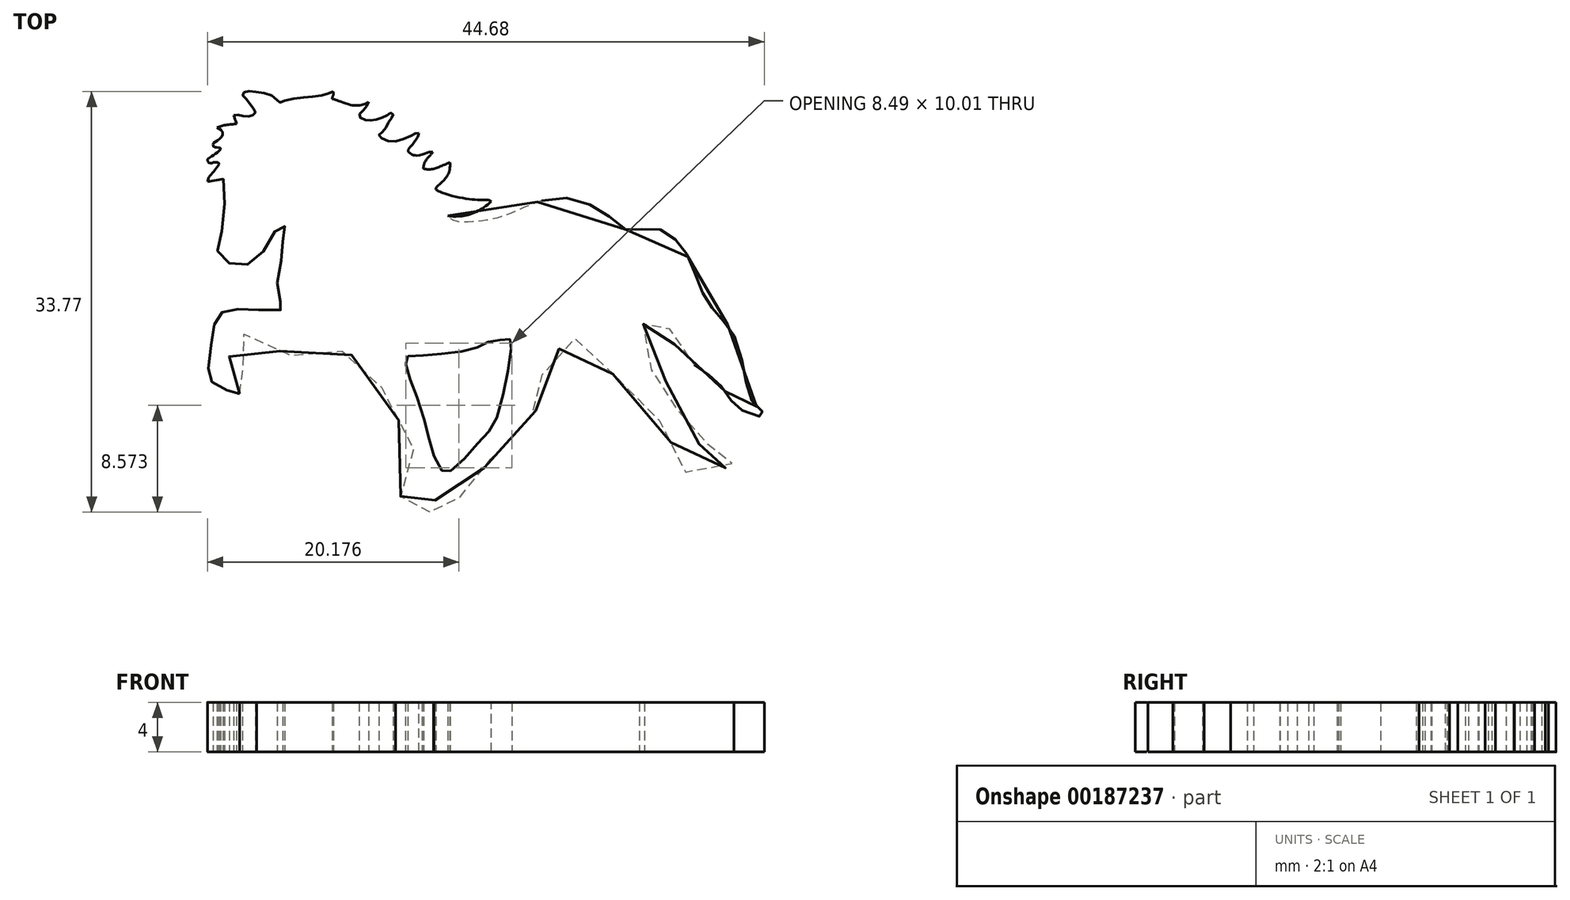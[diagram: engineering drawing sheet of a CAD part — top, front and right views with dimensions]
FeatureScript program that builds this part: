
annotation { "Feature Type Name" : "Feature", "Feature Type Description" : "" }
export const myFeature = defineFeature(function(context is Context, id is Id, definition is map)
    precondition{}
    {
        {
            var Q0;
            Q0=qCreatedBy(makeId("Top.planeOp"),FACE);
            var sketch = newSketch(context, id + "F0", { "sketchPlane" : qUnion([Q0])});
            skFitSpline(sketch, "E0", {"points": [v(-19.66, -6.58) * mm, v(-19.32, -6.77) * mm, v(-19.06, -7) * mm, v(-18.68, -7.1) * mm, v(-18.52, -6.92) * mm, v(-18.36, -6.26) * mm, v(-18.3, -5.53) * mm, v(-18.34, -5.04) * mm, v(-18.59, -4.66) * mm, v(-18.96, -4.5) * mm, v(-19.4, -4.46) * mm, v(-19.84, -4.47) * mm, v(-20.16, -4.42) * mm, v(-20.37, -4.19) * mm, v(-20.5, -3.63) * mm, v(-20.47, -3.09) * mm, v(-20.4, -2.68) * mm, v(-20.28, -2.34) * mm, v(-20.1, -2.05) * mm, v(-19.86, -1.84) * mm, v(-19.46, -1.77) * mm, v(-19.01, -1.89) * mm, v(-18.56, -2.05) * mm, v(-18.29, -2.17) * mm, v(-18, -2.38) * mm, v(-17.85, -2.53) * mm, v(-17.7, -2.7) * mm, v(-17.3, -2.9) * mm, v(-16.9, -3) * mm, v(-16.5, -3.13) * mm, v(-16.05, -3.3) * mm, v(-15.55, -3.5) * mm, v(-15.04, -3.66) * mm, v(-14.53, -3.79) * mm, v(-14.04, -3.85) * mm, v(-13.73, -3.8) * mm, v(-13.44, -3.68) * mm, v(-13.23, -3.53) * mm, v(-12.9, -3.31) * mm, v(-12.53, -3.15) * mm, v(-12.05, -3.08) * mm, v(-11.55, -3.13) * mm, v(-11.17, -3.25) * mm, v(-10.8, -3.4) * mm, v(-10.48, -3.58) * mm, v(-10.2, -3.76) * mm, v(-9.77, -4.07) * mm, v(-9.46, -4.37) * mm, v(-9.16, -4.7) * mm, v(-8.95, -5) * mm, v(-8.7, -5.37) * mm, v(-8.37, -5.9) * mm, v(-8.04, -6.5) * mm, v(-8, -6.56) * mm, v(-7.75, -7.1) * mm, v(-7.43, -7.72) * mm, v(-7.13, -8.29) * mm, v(-6.89, -8.72) * mm, v(-6.35, -9.73) * mm, v(-5.99, -10.43) * mm, v(-5.58, -11.3) * mm, v(-5.29, -12.03) * mm, v(-5.13, -12.5) * mm, v(-5.04, -12.72) * mm, v(-5.03, -12.86) * mm, v(-5.07, -13.02) * mm, v(-5.18, -13.11) * mm, v(-5.63, -13.52) * mm, v(-6, -13.88) * mm, v(-6.39, -14.3) * mm, v(-6.72, -14.8) * mm, v(-6.93, -15.15) * mm, v(-7.05, -15.42) * mm, v(-7.13, -15.63) * mm, v(-7.13, -15.8) * mm, v(-7.06, -15.88) * mm, v(-6.91, -15.93) * mm, v(-6.69, -15.95) * mm, v(-6.1, -16.01) * mm, v(-5.61, -16.05) * mm, v(-5.05, -16.08) * mm, v(-4.67, -16.08) * mm, v(-4.4, -16.06) * mm, v(-4.2, -16) * mm, v(-4.12, -15.91) * mm, v(-4.08, -15.82) * mm, v(-4.1, -15.6) * mm, v(-4.08, -15.38) * mm, v(-4, -15.19) * mm, v(-3.86, -15.09) * mm, v(-3.68, -15.04) * mm, v(-3.31, -15.05) * mm, v(-2.9, -15.07) * mm, v(-2.58, -15.07) * mm, v(-2.37, -15.06) * mm, v(-2.19, -15.02) * mm, v(-2, -14.9) * mm, v(-1.86, -14.75) * mm, v(-1.74, -14.5) * mm, v(-1.63, -14.34) * mm, v(-1.44, -14.1) * mm, v(-1.16, -13.82) * mm, v(-0.91, -13.58) * mm, v(-0.62, -13.28) * mm, v(-0.4, -13.02) * mm, v(-0.18, -12.71) * mm, v(0.06, -12.39) * mm, v(0.26, -12.12) * mm, v(0.67, -11.57) * mm, v(1, -11.16) * mm, v(1.3, -10.8) * mm, v(1.65, -10.4) * mm, v(2.05, -9.96) * mm, v(2.35, -9.67) * mm, v(2.64, -9.36) * mm, v(3.07, -8.96) * mm, v(3.43, -8.66) * mm, v(3.85, -8.32) * mm, v(3.99, -8.22) * mm, v(4.06, -8.1) * mm, v(4.1, -7.96) * mm, v(4.16, -7.68) * mm, v(4.21, -7.36) * mm, v(4.28, -7.08) * mm, v(4.34, -6.81) * mm, v(4.35, -6.55) * mm, v(4.37, -6.21) * mm, v(4.42, -5.84) * mm, v(4.5, -5.56) * mm, v(4.59, -5.2) * mm, v(4.7, -4.85) * mm, v(4.86, -4.51) * mm, v(5, -4.22) * mm, v(5.17, -3.92) * mm, v(5.38, -3.62) * mm, v(5.65, -3.3) * mm, v(6.04, -2.91) * mm, v(6.35, -2.65) * mm, v(6.6, -2.46) * mm, v(6.84, -2.29) * mm, v(7.16, -2.17) * mm, v(7.33, -2.2) * mm, v(7.48, -2.3) * mm, v(7.62, -2.51) * mm, v(7.8, -2.77) * mm, v(8.05, -3.06) * mm, v(8.3, -3.34) * mm, v(8.55, -3.58) * mm, v(8.98, -3.95) * mm, v(9.37, -4.27) * mm, v(9.68, -4.51) * mm, v(10.18, -4.9) * mm, v(10.58, -5.22) * mm, v(10.95, -5.54) * mm, v(11.39, -5.93) * mm, v(11.84, -6.33) * mm, v(12.4, -6.86) * mm, v(12.94, -7.42) * mm, v(13.43, -7.97) * mm, v(13.8, -8.45) * mm, v(14.15, -8.95) * mm, v(14.46, -9.48) * mm, v(14.7, -9.94) * mm, v(14.92, -10.46) * mm, v(15.16, -11) * mm, v(15.37, -11.58) * mm, v(15.55, -12) * mm, v(15.75, -12.43) * mm, v(15.93, -12.67) * mm, v(16.07, -12.83) * mm, v(16.3, -12.95) * mm, v(16.54, -13.03) * mm, v(16.75, -13.05) * mm, v(17.06, -13.03) * mm, v(17.38, -13) * mm, v(17.96, -12.9) * mm, v(18.53, -12.77) * mm, v(19.08, -12.61) * mm, v(19.29, -12.54) * mm, v(19.53, -12.43) * mm, v(19.72, -12.3) * mm, v(19.86, -12.18) * mm, v(19.95, -12.07) * mm, v(20, -11.95) * mm, v(19.96, -11.85) * mm, v(19.88, -11.73) * mm, v(19.78, -11.61) * mm, v(19.44, -11.3) * mm, v(19.27, -11.16) * mm, v(19.05, -10.94) * mm, v(18.9, -10.78) * mm, v(18.75, -10.64) * mm, v(18.63, -10.58) * mm, v(18.52, -10.57) * mm, v(18.45, -10.56) * mm, v(18.26, -10.59) * mm, v(18.04, -10.63) * mm, v(17.73, -10.67) * mm, v(17.4, -10.65) * mm, v(17.14, -10.62) * mm, v(16.89, -10.52) * mm, v(16.61, -10.34) * mm, v(16.36, -10.12) * mm, v(16.16, -9.82) * mm, v(16.05, -9.56) * mm, v(15.93, -9.2) * mm, v(15.8, -8.8) * mm, v(15.7, -8.42) * mm, v(15.45, -7.59) * mm, v(15.2, -6.72) * mm, v(15.06, -6.12) * mm, v(14.97, -5.92) * mm, v(14.87, -5.79) * mm, v(14.76, -5.69) * mm, v(14.6, -5.62) * mm, v(14.37, -5.5) * mm, v(14.1, -5.34) * mm, v(13.82, -5.12) * mm, v(13.6, -4.9) * mm, v(13.37, -4.64) * mm, v(13.2, -4.42) * mm, v(13, -4.2) * mm, v(12.78, -3.92) * mm, v(12.66, -3.75) * mm, v(12.56, -3.57) * mm, v(12.47, -3.32) * mm, v(12.4, -2.97) * mm, v(12.46, -2.44) * mm, v(12.57, -1.84) * mm, v(12.65, -1.45) * mm, v(12.73, -1.04) * mm, v(12.79, -0.7) * mm, v(12.8, -0.37) * mm, v(12.83, 0) * mm, v(12.83, 0.2) * mm, v(12.83, 0.4) * mm, v(12.86, 0.42) * mm, v(13.16, 0.14) * mm, v(13.7, -0.35) * mm, v(14.26, -0.86) * mm, v(14.48, -1.06) * mm, v(14.66, -1.22) * mm, v(14.79, -1.34) * mm, v(14.88, -1.5) * mm, v(14.93, -1.7) * mm, v(14.98, -1.96) * mm, v(15.05, -2.2) * mm, v(15.2, -2.55) * mm, v(15.34, -2.82) * mm, v(15.52, -3.1) * mm, v(15.73, -3.35) * mm, v(15.94, -3.58) * mm, v(16.13, -3.75) * mm, v(16.4, -3.97) * mm, v(16.73, -4.2) * mm, v(17.04, -4.41) * mm, v(17.36, -4.63) * mm, v(17.63, -4.8) * mm, v(18.02, -5.1) * mm, v(18.27, -5.31) * mm, v(18.62, -5.6) * mm, v(18.88, -5.86) * mm, v(19.15, -6.18) * mm, v(19.38, -6.49) * mm, v(19.64, -6.89) * mm, v(19.77, -7.13) * mm, v(19.9, -7.3) * mm, v(20.04, -7.46) * mm, v(20.32, -7.7) * mm, v(20.63, -7.91) * mm, v(20.97, -8.07) * mm, v(21.39, -8.22) * mm, v(21.81, -8.34) * mm, v(22.12, -8.42) * mm, v(22.3, -8.4) * mm, v(22.4, -8.32) * mm, v(22.44, -8.24) * mm, v(22.44, -8.18) * mm, v(22.38, -8.1) * mm, v(22.3, -8.05) * mm, v(22.1, -7.9) * mm, v(21.88, -7.7) * mm, v(21.68, -7.48) * mm, v(21.46, -7.18) * mm, v(21.27, -6.85) * mm, v(21.15, -6.52) * mm, v(21.03, -6) * mm, v(20.93, -5.4) * mm, v(20.8, -4.67) * mm, v(20.66, -3.95) * mm, v(20.51, -3.33) * mm, v(20.19, -2.39) * mm, v(19.92, -1.7) * mm, v(19.7, -1.29) * mm, v(19.47, -1.01) * mm, v(19.2, -0.77) * mm, v(18.88, -0.47) * mm, v(18.75, -0.34) * mm, v(18.46, 0) * mm, v(18.13, 0.44) * mm, v(17.89, 0.8) * mm, v(17.68, 1.15) * mm, v(17.54, 1.4) * mm, v(17.23, 2.07) * mm, v(17.02, 2.6) * mm, v(16.8, 3.26) * mm, v(16.64, 3.75) * mm, v(16.5, 4.07) * mm, v(16.24, 4.55) * mm, v(16.02, 4.9) * mm, v(15.64, 5.39) * mm, v(15.43, 5.63) * mm, v(15.15, 5.95) * mm, v(14.82, 6.22) * mm, v(14.44, 6.44) * mm, v(14.01, 6.6) * mm, v(13.57, 6.67) * mm, v(13.1, 6.68) * mm, v(12.65, 6.63) * mm, v(12.28, 6.53) * mm, v(11.95, 6.47) * mm, v(11.62, 6.48) * mm, v(11.35, 6.57) * mm, v(10.91, 6.88) * mm, v(10.48, 7.26) * mm, v(9.97, 7.66) * mm, v(9.4, 8.05) * mm, v(8.87, 8.37) * mm, v(8.2, 8.72) * mm, v(7.53, 8.96) * mm, v(6.71, 9.12) * mm, v(6, 9.14) * mm, v(5.12, 9.04) * mm, v(4.27, 8.8) * mm, v(3.47, 8.5) * mm, v(2.77, 8.17) * mm, v(1.95, 7.83) * mm, v(1.14, 7.57) * mm, v(0.17, 7.34) * mm, v(-0.56, 7.24) * mm, v(-1.38, 7.19) * mm, v(-1.87, 7.18) * mm, v(-2.4, 7.29) * mm, v(-2.68, 7.43) * mm, v(-2.9, 7.59) * mm, v(-2.97, 7.7) * mm, v(-2.97, 7.7) * mm], "startDerivative": vector(127.66, -56.54) * mm, "endDerivative": vector(-6.3, 6.24) * mm});
            skFitSpline(sketch, "E1", {"points": [v(-2.97, 7.7) * mm, v(-2.38, 7.65) * mm, v(-1.73, 7.7) * mm, v(-1.1, 7.84) * mm, v(-0.44, 8.13) * mm, v(0.17, 8.53) * mm, v(0.52, 8.83) * mm, v(0.52, 8.83) * mm], "startDerivative": vector(3.64, -0.41) * mm, "endDerivative": vector(-0.04, 0.27) * mm});
            skFitSpline(sketch, "E2", {"points": [v(0.52, 8.83) * mm, v(0.44, 8.92) * mm, v(0.35, 8.95) * mm, v(0.23, 8.96) * mm, v(0, 8.96) * mm, v(-0.52, 8.97) * mm, v(-1.1, 9.01) * mm, v(-1.9, 9.14) * mm, v(-2.97, 9.39) * mm, v(-3.6, 9.63) * mm, v(-3.75, 9.69) * mm, v(-3.9, 9.8) * mm], "startDerivative": vector(-1.54, 1.79) * mm, "endDerivative": vector(-2.3, 1.89) * mm});
            skFitSpline(sketch, "E3", {"points": [v(-3.9, 9.8) * mm, v(-3.91, 9.83) * mm, v(-3.91, 9.88) * mm, v(-3.88, 9.98) * mm, v(-3.8, 10.06) * mm, v(-3.66, 10.19) * mm, v(-3.5, 10.33) * mm, v(-3.3, 10.52) * mm, v(-3.13, 10.71) * mm, v(-2.97, 10.97) * mm, v(-2.84, 11.28) * mm, v(-2.78, 11.6) * mm, v(-2.78, 11.98) * mm], "startDerivative": vector(-0.47, 0.94) * mm, "endDerivative": vector(-0.1, 3.39) * mm});
            skFitSpline(sketch, "E4", {"points": [v(-2.78, 11.98) * mm, v(-2.97, 11.9) * mm, v(-3.27, 11.77) * mm, v(-3.64, 11.62) * mm, v(-3.9, 11.53) * mm, v(-4.23, 11.43) * mm, v(-4.5, 11.41) * mm, v(-4.7, 11.43) * mm, v(-4.81, 11.45) * mm, v(-4.9, 11.48) * mm], "startDerivative": vector(-1.7, -0.76) * mm, "endDerivative": vector(-1.3, 0.34) * mm});
            skFitSpline(sketch, "E5", {"points": [v(-4.88, 11.47) * mm, v(-4.9, 11.48) * mm, v(-4.9, 11.6) * mm, v(-4.88, 11.78) * mm, v(-4.8, 12) * mm, v(-4.6, 12.3) * mm, v(-4.37, 12.55) * mm, v(-4.15, 12.8) * mm], "startDerivative": vector(-0.65, -0.02) * mm, "endDerivative": vector(1.22, 1.4) * mm});
            skFitSpline(sketch, "E6", {"points": [v(-4.15, 12.8) * mm, v(-4.27, 12.8) * mm, v(-4.49, 12.79) * mm, v(-4.72, 12.71) * mm, v(-4.93, 12.64) * mm, v(-5.35, 12.55) * mm, v(-5.58, 12.54) * mm, v(-5.7, 12.56) * mm, v(-5.84, 12.62) * mm, v(-5.91, 12.67) * mm, v(-6.06, 12.77) * mm, v(-6.13, 12.86) * mm, v(-6.15, 12.93) * mm, v(-6.13, 13.01) * mm, v(-6.07, 13.1) * mm, v(-5.95, 13.23) * mm, v(-5.86, 13.33) * mm, v(-5.75, 13.46) * mm, v(-5.47, 13.84) * mm, v(-5.32, 14.14) * mm, v(-5.27, 14.32) * mm, v(-5.27, 14.32) * mm], "startDerivative": vector(-2.78, 0.02) * mm, "endDerivative": vector(-0.04, 0.47) * mm});
            skFitSpline(sketch, "E7", {"points": [v(-5.27, 14.32) * mm, v(-5.34, 14.32) * mm, v(-5.43, 14.32) * mm, v(-5.55, 14.3) * mm, v(-5.66, 14.23) * mm, v(-5.84, 14.13) * mm, v(-6.25, 13.96) * mm, v(-6.75, 13.77) * mm, v(-7.21, 13.67) * mm, v(-7.65, 13.68) * mm, v(-7.97, 13.76) * mm, v(-8.31, 13.95) * mm, v(-8.42, 14.03) * mm, v(-8.47, 14.15) * mm, v(-8.43, 14.23) * mm, v(-8.3, 14.32) * mm, v(-8.15, 14.44) * mm, v(-8.02, 14.6) * mm, v(-7.85, 14.87) * mm, v(-7.75, 15.1) * mm, v(-7.66, 15.27) * mm, v(-7.55, 15.46) * mm, v(-7.4, 15.6) * mm, v(-7.33, 15.7) * mm, v(-7.34, 15.8) * mm, v(-7.4, 15.9) * mm, v(-7.47, 15.94) * mm, v(-7.53, 15.95) * mm, v(-7.59, 15.93) * mm, v(-7.65, 15.89) * mm, v(-7.74, 15.81) * mm, v(-7.86, 15.73) * mm, v(-8.09, 15.63) * mm, v(-8.39, 15.51) * mm, v(-8.65, 15.42) * mm, v(-8.9, 15.36) * mm, v(-9.13, 15.34) * mm, v(-9.3, 15.35) * mm, v(-9.53, 15.37) * mm, v(-9.8, 15.46) * mm, v(-9.99, 15.58) * mm, v(-10.06, 15.67) * mm, v(-10.06, 15.82) * mm, v(-10, 15.91) * mm, v(-9.84, 16.08) * mm, v(-9.66, 16.24) * mm, v(-9.55, 16.37) * mm, v(-9.43, 16.55) * mm, v(-9.36, 16.72) * mm, v(-9.32, 16.83) * mm], "startDerivative": vector(-4.95, -0.07) * mm, "endDerivative": vector(1.99, 6.47) * mm});
            skFitSpline(sketch, "E8", {"points": [v(-9.32, 16.83) * mm, v(-9.4, 16.78) * mm, v(-9.51, 16.71) * mm, v(-9.72, 16.63) * mm, v(-9.9, 16.57) * mm, v(-10.16, 16.55) * mm, v(-10.51, 16.55) * mm, v(-10.94, 16.64) * mm, v(-11.48, 16.83) * mm, v(-11.67, 16.9) * mm, v(-11.95, 16.99) * mm, v(-12.02, 17.02) * mm, v(-12.18, 17.07) * mm, v(-12.21, 17.08) * mm], "startDerivative": vector(-1.36, -0.92) * mm, "endDerivative": vector(-0.88, 0.2) * mm});
            skFitSpline(sketch, "E9", {"points": [v(-12.2, 17.08) * mm, v(-12.21, 17.08) * mm, v(-12.22, 17.13) * mm, v(-12.2, 17.24) * mm, v(-12.17, 17.33) * mm, v(-12.13, 17.43) * mm, v(-12.12, 17.52) * mm, v(-12.15, 17.63) * mm, v(-12.17, 17.67) * mm], "startDerivative": vector(-0.23, -0.01) * mm, "endDerivative": vector(-0.22, 0.27) * mm});
            skFitSpline(sketch, "E10", {"points": [v(-12.17, 17.67) * mm, v(-12.21, 17.64) * mm, v(-12.32, 17.6) * mm, v(-12.52, 17.51) * mm, v(-12.7, 17.45) * mm, v(-13.1, 17.35) * mm, v(-13.57, 17.27) * mm, v(-14.04, 17.23) * mm, v(-14.5, 17.2) * mm, v(-15.08, 17.13) * mm, v(-15.65, 17.03) * mm, v(-16.05, 16.92) * mm, v(-16.22, 16.85) * mm, v(-16.35, 16.8) * mm, v(-16.44, 16.79) * mm, v(-16.52, 16.83) * mm, v(-16.6, 16.92) * mm, v(-16.67, 17) * mm, v(-16.88, 17.2) * mm, v(-17.13, 17.36) * mm, v(-17.5, 17.5) * mm, v(-17.84, 17.58) * mm, v(-18.26, 17.63) * mm, v(-18.56, 17.65) * mm, v(-18.84, 17.68) * mm, v(-19.1, 17.68) * mm, v(-19.21, 17.65) * mm, v(-19.29, 17.61) * mm, v(-19.36, 17.54) * mm, v(-19.4, 17.46) * mm, v(-19.41, 17.38) * mm, v(-19.38, 17.3) * mm, v(-19.28, 17.2) * mm, v(-19.17, 17.12) * mm, v(-19.1, 17.04) * mm, v(-19.03, 16.93) * mm, v(-18.86, 16.7) * mm, v(-18.66, 16.44) * mm, v(-18.57, 16.35) * mm, v(-18.46, 16.25) * mm, v(-18.4, 16.15) * mm, v(-18.38, 16.01) * mm, v(-18.4, 15.93) * mm, v(-18.46, 15.85) * mm, v(-18.55, 15.78) * mm, v(-18.66, 15.74) * mm, v(-18.75, 15.7) * mm, v(-18.9, 15.68) * mm, v(-19.05, 15.67) * mm, v(-19.18, 15.67) * mm, v(-19.34, 15.7) * mm, v(-19.5, 15.73) * mm, v(-19.66, 15.77) * mm, v(-19.8, 15.8) * mm, v(-19.97, 15.8) * mm, v(-20.1, 15.77) * mm, v(-20.14, 15.76) * mm], "startDerivative": vector(-4.11, -2.4) * mm, "endDerivative": vector(-4.12, -1.45) * mm});
            skFitSpline(sketch, "E11", {"points": [v(-20.14, 15.76) * mm, v(-19.9, 15.14) * mm, v(-19.9, 15.1) * mm, v(-19.97, 15.07) * mm, v(-20.18, 15.04) * mm, v(-20.65, 15) * mm, v(-21.1, 14.9) * mm, v(-21.48, 14.78) * mm], "startDerivative": vector(1.37, -3.66) * mm, "endDerivative": vector(-2.16, -0.83) * mm});
            skFitSpline(sketch, "E12", {"points": [v(-21.48, 14.78) * mm, v(-21.33, 14.7) * mm, v(-21.1, 14.54) * mm, v(-21, 14.32) * mm, v(-21.06, 14.1) * mm, v(-21.16, 13.95) * mm, v(-21.44, 13.74) * mm, v(-21.6, 13.64) * mm, v(-21.74, 13.53) * mm, v(-21.78, 13.46) * mm, v(-21.79, 13.33) * mm, v(-21.73, 13.23) * mm, v(-21.64, 13.2) * mm, v(-21.51, 13.19) * mm, v(-21.33, 13.17) * mm, v(-21.25, 13.14) * mm, v(-21.19, 13.1) * mm, v(-21.18, 13.05) * mm, v(-21.24, 12.98) * mm, v(-21.37, 12.85) * mm, v(-21.53, 12.71) * mm, v(-21.7, 12.6) * mm, v(-21.88, 12.47) * mm, v(-22.1, 12.34) * mm, v(-22.24, 12.25) * mm], "startDerivative": vector(3.3, -1.77) * mm, "endDerivative": vector(-3.27, -1.95) * mm});
            skFitSpline(sketch, "E13", {"points": [v(-22.24, 12.25) * mm, v(-22.24, 12.17) * mm, v(-22.2, 12.03) * mm, v(-22.1, 11.94) * mm, v(-21.95, 11.92) * mm, v(-21.77, 11.98) * mm, v(-21.62, 12) * mm, v(-21.48, 12) * mm, v(-21.36, 11.94) * mm, v(-21.32, 11.88) * mm, v(-21.32, 11.8) * mm, v(-21.45, 11.62) * mm, v(-21.6, 11.4) * mm, v(-21.7, 11.26) * mm, v(-21.88, 11.07) * mm, v(-22.02, 10.91) * mm, v(-22.14, 10.75) * mm, v(-22.2, 10.6) * mm, v(-22.21, 10.42) * mm, v(-22.21, 10.42) * mm], "startDerivative": vector(-0.16, -1.95) * mm, "endDerivative": vector(-0.4, 0.21) * mm});
            skFitSpline(sketch, "E14", {"points": [v(-22.21, 10.42) * mm, v(-21.66, 10.54) * mm, v(-21.33, 10.61) * mm, v(-21.1, 10.66) * mm, v(-20.97, 10.64) * mm, v(-20.9, 10.55) * mm, v(-20.88, 10.45) * mm, v(-20.86, 9.28) * mm, v(-20.89, 7.94) * mm, v(-20.99, 6.96) * mm, v(-21.15, 6.17) * mm, v(-21.37, 5.49) * mm, v(-21.44, 5.1) * mm, v(-21.4, 4.83) * mm, v(-21.25, 4.58) * mm, v(-20.96, 4.3) * mm, v(-20.6, 3.97) * mm, v(-20.28, 3.76) * mm, v(-19.93, 3.62) * mm, v(-19.4, 3.66) * mm, v(-18.79, 3.88) * mm, v(-18.28, 4.22) * mm, v(-17.95, 4.56) * mm, v(-17.57, 5.13) * mm, v(-17.25, 5.75) * mm, v(-16.91, 6.32) * mm, v(-16.6, 6.7) * mm, v(-16.44, 6.86) * mm, v(-16.28, 6.96) * mm, v(-16.13, 6.96) * mm, v(-16.04, 6.86) * mm, v(-16.03, 6.7) * mm, v(-16.09, 6.51) * mm, v(-16.15, 6.22) * mm, v(-16.18, 5.77) * mm, v(-16.2, 5.27) * mm, v(-16.22, 4.78) * mm, v(-16.3, 4.25) * mm, v(-16.45, 3.63) * mm, v(-16.61, 2.65) * mm, v(-16.64, 2.36) * mm, v(-16.65, 1.94) * mm, v(-16.57, 1.3) * mm, v(-16.45, 0.92) * mm, v(-16.36, 0.7) * mm, v(-16.28, 0.53) * mm, v(-16.22, 0.42) * mm, v(-16.2, 0.26) * mm, v(-16.24, 0.18) * mm, v(-16.3, 0.15) * mm, v(-16.4, 0.14) * mm, v(-16.56, 0.15) * mm, v(-17.27, 0.18) * mm, v(-18.17, 0.15) * mm, v(-18.98, 0.13) * mm, v(-19.41, 0.15) * mm, v(-19.8, 0.22) * mm, v(-20.23, 0.24) * mm, v(-20.61, 0.18) * mm, v(-20.87, 0.08) * mm, v(-21.14, -0.1) * mm, v(-21.36, -0.32) * mm, v(-21.53, -0.58) * mm, v(-21.63, -0.8) * mm, v(-21.69, -1.1) * mm, v(-21.72, -1.34) * mm, v(-21.86, -2.2) * mm, v(-21.93, -2.74) * mm, v(-22.04, -3.57) * mm, v(-22.13, -4.2) * mm, v(-22.2, -4.8) * mm, v(-22.21, -5.2) * mm, v(-22.15, -5.43) * mm, v(-22, -5.6) * mm, v(-21.73, -5.68) * mm, v(-21.36, -5.9) * mm, v(-21.05, -6.08) * mm, v(-20.74, -6.28) * mm, v(-20.36, -6.45) * mm, v(-20.19, -6.51) * mm, v(-20.02, -6.53) * mm, v(-19.8, -6.55) * mm, v(-19.66, -6.58) * mm], "startDerivative": vector(39.68, 8.56) * mm, "endDerivative": vector(17.3, -4.59) * mm});
            skFitSpline(sketch, "E15", {"points": [v(-6.31, -4.22) * mm, v(-6.2, -4.8) * mm, v(-5.91, -5.61) * mm, v(-5.56, -6.5) * mm, v(-5.06, -7.96) * mm, v(-4.68, -9.3) * mm, v(-4.43, -10.37) * mm, v(-4.23, -11.15) * mm, v(-3.83, -12.1) * mm, v(-3.5, -12.67) * mm, v(-3.24, -12.9) * mm, v(-3, -12.92) * mm, v(-2.73, -12.76) * mm, v(-2.02, -12.2) * mm, v(-1.26, -11.38) * mm, v(-0.51, -10.53) * mm, v(0, -9.96) * mm, v(0.58, -9.38) * mm, v(0.85, -8.88) * mm, v(1.28, -7.37) * mm, v(1.68, -5.86) * mm, v(1.96, -4.17) * mm, v(2.15, -2.92) * mm, v(2.18, -2.55) * mm, v(2.13, -2.33) * mm, v(1.98, -2.2) * mm, v(1.8, -2.17) * mm, v(1.47, -2.24) * mm, v(1.1, -2.31) * mm, v(0.65, -2.37) * mm, v(0.24, -2.45) * mm, v(-0.1, -2.59) * mm, v(-0.46, -2.8) * mm, v(-1.1, -3.06) * mm, v(-1.86, -3.2) * mm, v(-3, -3.35) * mm, v(-4.2, -3.45) * mm, v(-5, -3.5) * mm, v(-5.87, -3.55) * mm, v(-6.2, -3.6) * mm, v(-6.33, -3.77) * mm, v(-6.35, -4) * mm, v(-6.31, -4.22) * mm]});
            skSolve(sketch);
        }
        {
            var Q0;
            Q0 = qSketchRegion(id + "F0", true);
            extrude(context, id + "F1", {"entities" : qUnion([Q0]), "endBound" : BoundingType.SYMMETRIC, "depth" : 4 * mm});
        }
    });
